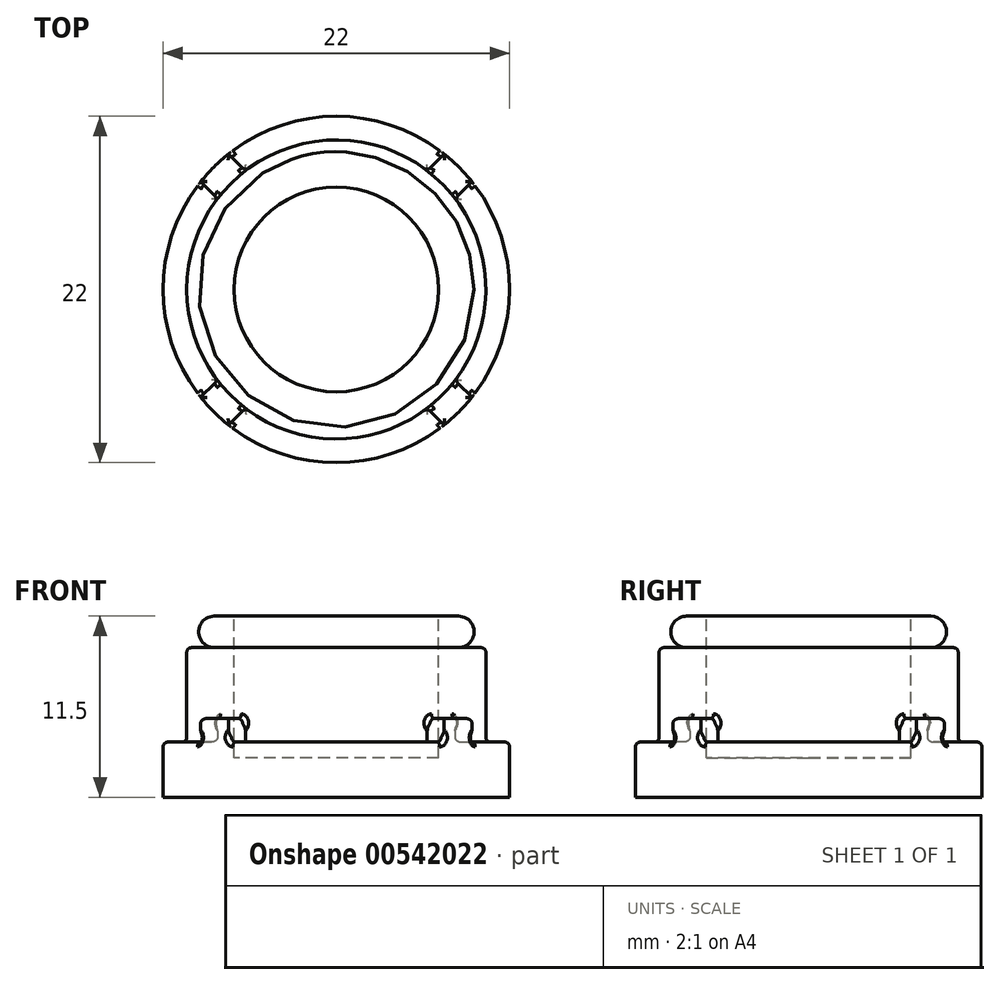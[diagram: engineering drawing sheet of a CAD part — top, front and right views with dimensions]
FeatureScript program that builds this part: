
annotation { "Feature Type Name" : "Feature", "Feature Type Description" : "" }
export const myFeature = defineFeature(function(context is Context, id is Id, definition is map)
    precondition{}
    {
        {
            var Q0;
            Q0=qCreatedBy(makeId("Top.planeOp"),FACE);
            var sketch = newSketch(context, id + "F0", { "sketchPlane" : qUnion([Q0])});
            skCircle(sketch, "E0", {"center": v(0, 0) * mm, "radius": 6.5 * mm});
            skSolve(sketch);
        }
        {
            var Q0;
            Q0=qSketchRegion(id+"F0",true);
            extrude(context, id + "F1", {"entities" : qUnion([Q0]), "oppositeDirection" : true, "depth" : 9 * mm});
        }
        {
            var Q0;
            Q0=qCreatedBy(makeId("Top.planeOp"),FACE);
            var sketch = newSketch(context, id + "F2", { "sketchPlane" : qUnion([Q0])});
            skCircle(sketch, "E1", {"center": v(0, 0) * mm, "radius": 8.75 * mm});
            skSolve(sketch);
        }
        {
            var Q0;
            Q0=qSketchRegion(id+"F2",true);
            extrude(context, id + "F3", {"entities" : qUnion([Q0]), "oppositeDirection" : true, "depth" : 2 * mm});
        }
        {
            var Q0;
            Q0=makeQuery(id+"F3.opExtrude","CAP_EDGE",EDGE,{"disambiguationData":[OSD([sQuery(id+"F2.wireOp",EDGE,"E1")])],"isStart":false});
            var Q1;
            Q1=makeQuery(id+"F3.opExtrude","CAP_EDGE",EDGE,{"disambiguationData":[OSD([sQuery(id+"F2.wireOp",EDGE,"E1")])],"isStart":true});
            fillet(context, id + "F4", {"entities" : qUnion([Q0, Q1]), "radius" : 1 * mm, "tangentPropagation" : true, "allowEdgeOverflow" : false});
        }
        {
            var Q0;
            Q0=makeQuery(id+"F3.opExtrude","CAP_FACE",FACE,{"disambiguationData":[OSD([sQuery(id+"F2.wireOp",EDGE,"E1")])],"isStart":false});
            var sketch = newSketch(context, id + "F5", { "sketchPlane" : qUnion([Q0])});
            skCircle(sketch, "E2", {"center": v(0, 0) * mm, "radius": 9.5 * mm});
            skSolve(sketch);
        }
        {
            var Q0;
            Q0=qSketchRegion(id+"F5",true);
            extrude(context, id + "F6", {"entities" : qUnion([Q0]), "depth" : 6 * mm});
        }
        {
            var Q0;
            Q0=makeQuery(id+"F6.opExtrude","CAP_FACE",FACE,{"disambiguationData":[OSD([sQuery(id+"F5.wireOp",EDGE,"E2")])],"isStart":false});
            var sketch = newSketch(context, id + "F7", { "sketchPlane" : qUnion([Q0])});
            skCircle(sketch, "E3", {"center": v(0, 0) * mm, "radius": 11 * mm});
            skSolve(sketch);
        }
        {
            var Q0;
            Q0=qSketchRegion(id+"F7",true);
            extrude(context, id + "F8", {"entities" : qUnion([Q0]), "depth" : 3.5 * mm});
        }
        {
            var Q0;
            Q0=makeQuery(id+"F8.opExtrude","CAP_FACE",FACE,{"disambiguationData":[OSD([sQuery(id+"F7.wireOp",EDGE,"E3")])],"isStart":true});
            var sketch = newSketch(context, id + "F9", { "sketchPlane" : qUnion([Q0])});
            skLineSegment(sketch, "E4.bottom", {"start": v(7.78, 7.78) * mm, "end": v(-7.78, 7.78) * mm, "construction": true});
            skLineSegment(sketch, "E4.top", {"start": v(7.78, -7.78) * mm, "end": v(-7.78, -7.78) * mm, "construction": true});
            skLineSegment(sketch, "E4.left", {"start": v(7.78, 7.78) * mm, "end": v(7.78, -7.78) * mm, "construction": true});
            skLineSegment(sketch, "E4.right", {"start": v(-7.78, 7.78) * mm, "end": v(-7.78, -7.78) * mm, "construction": true});
            skPoint(sketch, "E4.middle", {"position": v(0, 0) * mm});
            skLineSegment(sketch, "E5", {"start": v(-7.78, -7.78) * mm, "end": v(7.78, 7.78) * mm, "construction": true});
            skLineSegment(sketch, "E6", {"start": v(-7.78, 7.78) * mm, "end": v(7.78, -7.78) * mm, "construction": true});
            skLineSegment(sketch, "E7.0", {"start": v(-6.84, -8.61) * mm, "end": v(-5.78, -7.54) * mm});
            skLineSegment(sketch, "E8.0", {"start": v(-8.61, -6.84) * mm, "end": v(-7.54, -5.78) * mm});
            skLineSegment(sketch, "E9.0", {"start": v(-8.61, 6.84) * mm, "end": v(-7.54, 5.78) * mm});
            skLineSegment(sketch, "E10.0", {"start": v(-6.84, 8.61) * mm, "end": v(-5.78, 7.54) * mm});
            skArc(sketch, "E11.0", {"start": v(-6.84, 8.61) * mm, "mid": v(-7.78, 7.78) * mm, "end": v(-8.61, 6.84) * mm});
            skArc(sketch, "E12.trimOffspring", {"start": v(-8.61, -6.84) * mm, "mid": v(-7.78, -7.78) * mm, "end": v(-6.84, -8.61) * mm});
            skArc(sketch, "E13.trimOffspring", {"start": v(6.84, -8.61) * mm, "mid": v(7.78, -7.78) * mm, "end": v(8.61, -6.84) * mm});
            skArc(sketch, "E14.trimOffspring", {"start": v(8.61, 6.84) * mm, "mid": v(7.78, 7.78) * mm, "end": v(6.84, 8.61) * mm});
            skArc(sketch, "E15.0", {"start": v(-5.45, 7.78) * mm, "mid": v(-6.72, 6.72) * mm, "end": v(-7.78, 5.45) * mm});
            skArc(sketch, "E16.trimOffspring", {"start": v(7.78, 5.45) * mm, "mid": v(6.72, 6.72) * mm, "end": v(5.45, 7.78) * mm});
            skArc(sketch, "E17.trimOffspring", {"start": v(-7.78, -5.45) * mm, "mid": v(-6.72, -6.72) * mm, "end": v(-5.45, -7.78) * mm});
            skArc(sketch, "E18.trimOffspring", {"start": v(5.45, -7.78) * mm, "mid": v(6.72, -6.72) * mm, "end": v(7.78, -5.45) * mm});
            skLineSegment(sketch, "E19.trimOffspring", {"start": v(0, -1.77) * mm, "end": v(1.77, 0) * mm});
            skLineSegment(sketch, "E20.trimOffspring", {"start": v(-1.77, 0) * mm, "end": v(0, 1.77) * mm});
            skLineSegment(sketch, "E21.trimOffspring", {"start": v(5.78, -7.54) * mm, "end": v(6.84, -8.61) * mm});
            skLineSegment(sketch, "E22.trimOffspring", {"start": v(7.54, -5.78) * mm, "end": v(8.61, -6.84) * mm});
            skLineSegment(sketch, "E23.trimOffspring", {"start": v(7.54, 5.78) * mm, "end": v(8.61, 6.84) * mm});
            skLineSegment(sketch, "E24.trimOffspring", {"start": v(5.78, 7.54) * mm, "end": v(6.84, 8.61) * mm});
            skLineSegment(sketch, "E25.trimOffspring", {"start": v(0, 1.77) * mm, "end": v(1.77, 0) * mm});
            skLineSegment(sketch, "E26.trimOffspring", {"start": v(-1.77, 0) * mm, "end": v(0, -1.77) * mm});
            skSolve(sketch);
        }
        {
            var Q0;
            Q0=makeQuery(id+"F9.imprint","IMPRINT",FACE,{"disambiguationData":[TD([[makeQuery(id+"F9.imprint","IMPRINT",EDGE,{"derivedFrom":sQuery(id+"F9.wireOp",EDGE,"E13.trimOffspring")}),-1.0]])]});
            var Q1;
            Q1=makeQuery(id+"F9.imprint","IMPRINT",FACE,{"disambiguationData":[TD([[makeQuery(id+"F9.imprint","IMPRINT",EDGE,{"derivedFrom":sQuery(id+"F9.wireOp",EDGE,"E14.trimOffspring")}),-1.0]])]});
            var Q2;
            {var subQ0=sQuery(id+"F9.wireOp",EDGE,"E9.0");Q2=makeQuery(id+"F9.imprint","IMPRINT",FACE,{"disambiguationData":[TD([[makeQuery(id+"F9.imprint","IMPRINT",EDGE,{"derivedFrom":subQ0}),1.0]])]});}
            var Q3;
            {var subQ0=sQuery(id+"F9.wireOp",EDGE,"E7.0");Q3=makeQuery(id+"F9.imprint","IMPRINT",FACE,{"disambiguationData":[TD([[makeQuery(id+"F9.imprint","IMPRINT",EDGE,{"derivedFrom":subQ0}),1.0]])]});}
            extrude(context, id + "F10", {"entities" : qUnion([Q0, Q1, Q2, Q3]), "operationType" : NewBodyOperationType.ADD, "depth" : 1.5 * mm});
        }
        {
            var Q0;
            Q0=makeQuery(id+"F6.opExtrude","CAP_EDGE",EDGE,{"disambiguationData":[OSD([sQuery(id+"F5.wireOp",EDGE,"E2")])],"isStart":true});
            var Q1;
            Q1=makeQuery(id+"F10.opExtrude","CAP_FACE",FACE,{"disambiguationData":[OSD([sQuery(id+"F9.wireOp",EDGE,"E7.0"),sQuery(id+"F9.wireOp",EDGE,"E8.0"),sQuery(id+"F9.wireOp",EDGE,"E12.trimOffspring"),sQuery(id+"F9.wireOp",EDGE,"E17.trimOffspring")])],"isStart":false});
            var Q2;
            Q2=makeQuery(id+"F10.opExtrude","CAP_FACE",FACE,{"disambiguationData":[OSD([sQuery(id+"F9.wireOp",EDGE,"E13.trimOffspring"),sQuery(id+"F9.wireOp",EDGE,"E18.trimOffspring"),sQuery(id+"F9.wireOp",EDGE,"E21.trimOffspring"),sQuery(id+"F9.wireOp",EDGE,"E22.trimOffspring")])],"isStart":false});
            var Q3;
            Q3=makeQuery(id+"F8.opExtrude","CAP_FACE",FACE,{"disambiguationData":[OSD([sQuery(id+"F7.wireOp",EDGE,"E3")])],"isStart":true});
            var Q4;
            Q4=makeQuery(id+"F10.opExtrude","CAP_FACE",FACE,{"disambiguationData":[OSD([sQuery(id+"F9.wireOp",EDGE,"E9.0"),sQuery(id+"F9.wireOp",EDGE,"E10.0"),sQuery(id+"F9.wireOp",EDGE,"E11.0"),sQuery(id+"F9.wireOp",EDGE,"E15.0")])],"isStart":false});
            var Q5;
            Q5=makeQuery(id+"F10.opExtrude","CAP_EDGE",EDGE,{"disambiguationData":[OSD([sQuery(id+"F9.wireOp",EDGE,"E16.trimOffspring")])],"isStart":false});
            var Q6;
            Q6=makeQuery(id+"F10.opExtrude","CAP_FACE",FACE,{"disambiguationData":[OSD([sQuery(id+"F9.wireOp",EDGE,"E14.trimOffspring"),sQuery(id+"F9.wireOp",EDGE,"E16.trimOffspring"),sQuery(id+"F9.wireOp",EDGE,"E23.trimOffspring"),sQuery(id+"F9.wireOp",EDGE,"E24.trimOffspring")])],"isStart":false});
            fillet(context, id + "F11", {"entities" : qUnion([Q0, Q1, Q2, Q3, Q4, Q5, Q6]), "radius" : .3 * mm, "tangentPropagation" : true, "allowEdgeOverflow" : false});
        }
    });
